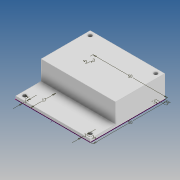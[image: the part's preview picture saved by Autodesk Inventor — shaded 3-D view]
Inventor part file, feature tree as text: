
AUTODESK INVENTOR PART (.ipt)
format: ipt  version: 2020 (Build 240168000, 168)  size: 267,264 bytes
history: native  units: mm
features: extrude x2, other x1, sketch x1, hole x1, shell x1
ambient origin geometry x8: Origin, YZ Plane, XZ Plane, XY Plane, X Axis, Y Axis, Z Axis, Center Point
bodies: Body1 (feature_tree)
feature tree (6):
  other  "솔리드1"
  sketch  "스케치1"
  extrude  "돌출1"  Depth=50.0mm
  extrude  "돌출2"  Depth=50.0mm
  hole  "구멍1"  [1 undecoded]
  shell  "쉘1"  Thickness=2.0mm
note: 1 required parameter value undecoded (feature->parameter linkage not recoverable at this tier; creation-order binding heuristic only, values carry confidence <= 0.55)
